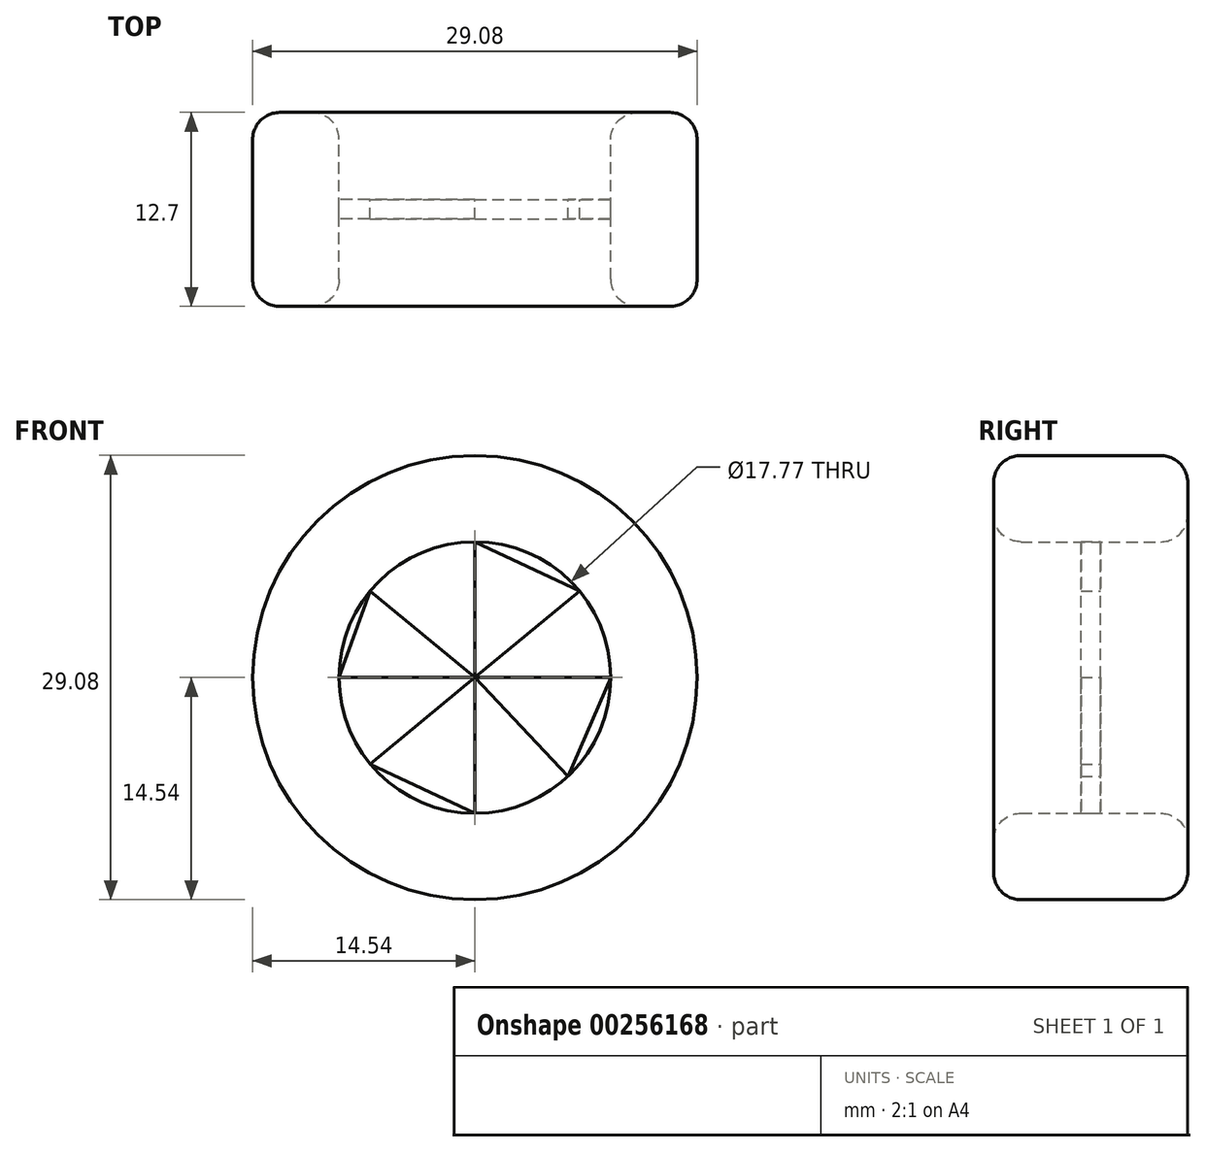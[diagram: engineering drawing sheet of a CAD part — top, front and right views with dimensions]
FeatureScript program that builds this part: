
annotation { "Feature Type Name" : "Feature", "Feature Type Description" : "" }
export const myFeature = defineFeature(function(context is Context, id is Id, definition is map)
    precondition{}
    {
        {
            var Q0;
            Q0=qCreatedBy(makeId("Front.planeOp"),FACE);
            var sketch = newSketch(context, id + "F0", { "sketchPlane" : qUnion([Q0])});
            skCircle(sketch, "E0", {"center": v(0, 0) * mm, "radius": 19.05 * mm});
            skCircle(sketch, "E1", {"center": v(0, 0) * mm, "radius": 8.9 * mm});
            skLineSegment(sketch, "E2", {"start": v(0, -8.9) * mm, "end": v(0, 0) * mm});
            skLineSegment(sketch, "E3", {"start": v(8.9, 0) * mm, "end": v(6.1, -6.48) * mm});
            skLineSegment(sketch, "E4", {"start": v(6.1, -6.48) * mm, "end": v(0, -8.9) * mm});
            skLineSegment(sketch, "E5", {"start": v(0, 0) * mm, "end": v(-8.9, 0) * mm});
            skLineSegment(sketch, "E6", {"start": v(-8.9, 0) * mm, "end": v(-6.85, -5.66) * mm});
            skLineSegment(sketch, "E7", {"start": v(-6.85, -5.66) * mm, "end": v(0, -8.9) * mm});
            skLineSegment(sketch, "E8", {"start": v(0, 0) * mm, "end": v(0, 8.9) * mm});
            skLineSegment(sketch, "E9", {"start": v(0, 8.9) * mm, "end": v(-6.85, 5.66) * mm});
            skLineSegment(sketch, "E10", {"start": v(-6.85, 5.66) * mm, "end": v(-8.9, 0) * mm});
            skLineSegment(sketch, "E11", {"start": v(0, 8.9) * mm, "end": v(6.85, 5.66) * mm});
            skLineSegment(sketch, "E12", {"start": v(6.85, 5.66) * mm, "end": v(8.89, 0) * mm});
            skLineSegment(sketch, "E13", {"start": v(0, 0) * mm, "end": v(8.89, 0) * mm});
            skLineSegment(sketch, "E14", {"start": v(0, 0) * mm, "end": v(6.1, -6.48) * mm});
            skLineSegment(sketch, "E15", {"start": v(0, 0) * mm, "end": v(6.85, 5.66) * mm});
            skLineSegment(sketch, "E16", {"start": v(-6.85, 5.66) * mm, "end": v(0, 0) * mm});
            skLineSegment(sketch, "E17", {"start": v(-6.85, -5.66) * mm, "end": v(0, 0) * mm});
            skSolve(sketch);
        }
        {
            var Q0;
            Q0=makeQuery(id+"F0.imprint","IMPRINT",FACE,{"disambiguationData":[TD([[makeQuery(id+"F0.imprint","IMPRINT",EDGE,{"derivedFrom":sQuery(id+"F0.wireOp",EDGE,"E5")}),-1.0]])]});
            var Q1;
            Q1=makeQuery(id+"F0.imprint","IMPRINT",FACE,{"disambiguationData":[TD([[makeQuery(id+"F0.imprint","IMPRINT",EDGE,{"derivedFrom":sQuery(id+"F0.wireOp",EDGE,"E2")}),1.0]])]});
            var Q2;
            Q2=makeQuery(id+"F0.imprint","IMPRINT",FACE,{"disambiguationData":[TD([[makeQuery(id+"F0.imprint","IMPRINT",EDGE,{"derivedFrom":sQuery(id+"F0.wireOp",EDGE,"E3")}),-1.0]])]});
            var Q3;
            Q3=makeQuery(id+"F0.imprint","IMPRINT",FACE,{"disambiguationData":[TD([[makeQuery(id+"F0.imprint","IMPRINT",EDGE,{"derivedFrom":sQuery(id+"F0.wireOp",EDGE,"E8")}),-1.0]])]});
            extrude(context, id + "F1", {"entities" : qUnion([Q0, Q1, Q2, Q3]), "endBound" : BoundingType.SYMMETRIC, "depth" : 1.27 * mm});
        }
        {
            var Q0;
            Q0=qCreatedBy(makeId("Front.planeOp"),FACE);
            var sketch = newSketch(context, id + "F2", { "sketchPlane" : qUnion([Q0])});
            skCircle(sketch, "E18", {"center": v(0, 0) * mm, "radius": 8.88 * mm});
            skCircle(sketch, "E19", {"center": v(0, 0) * mm, "radius": 14.54 * mm});
            skSolve(sketch);
        }
        {
            var Q0;
            Q0=makeQuery(id+"F2.imprint","IMPRINT",FACE,{"disambiguationData":[TD([[makeQuery(id+"F2.imprint","IMPRINT",EDGE,{"derivedFrom":sQuery(id+"F2.wireOp",EDGE,"E18")}),-1.0]])]});
            extrude(context, id + "F3", {"entities" : qUnion([Q0]), "endBound" : BoundingType.SYMMETRIC, "depth" : 12.7 * mm});
        }
        {
            var Q0;
            Q0=makeQuery(id+"F3.opExtrude","CAP_EDGE",EDGE,{"disambiguationData":[OSD([sQuery(id+"F2.wireOp",EDGE,"E19")])],"isStart":true});
            var Q1;
            Q1=makeQuery(id+"F3.opExtrude","CAP_EDGE",EDGE,{"disambiguationData":[OSD([sQuery(id+"F2.wireOp",EDGE,"E19")])],"isStart":false});
            var Q2;
            Q2=makeQuery(id+"F3.opExtrude","CAP_EDGE",EDGE,{"disambiguationData":[OSD([sQuery(id+"F2.wireOp",EDGE,"E18")])],"isStart":true});
            var Q3;
            Q3=makeQuery(id+"F3.opExtrude","CAP_EDGE",EDGE,{"disambiguationData":[OSD([sQuery(id+"F2.wireOp",EDGE,"E18")])],"isStart":false});
            fillet(context, id + "F4", {"entities" : qUnion([Q0, Q1, Q2, Q3]), "radius" : 1.78 * mm, "tangentPropagation" : true, "allowEdgeOverflow" : false});
        }
    });
